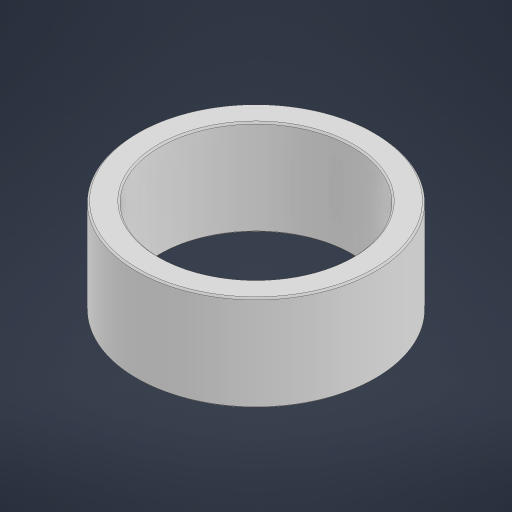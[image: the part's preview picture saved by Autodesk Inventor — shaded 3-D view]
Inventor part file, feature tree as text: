
AUTODESK INVENTOR PART (.ipt)
format: ipt  version: 2023 (Build 270158000, 158)  size: 179,712 bytes
history: native  units: in
note: dims shown in document units (in); Inventor stores cm internally (conversion verified against a paired STEP export)
features: chamfer x1
ambient origin geometry x8: Origin, YZ Plane, XZ Plane, XY Plane, X Axis, Y Axis, Z Axis, Center Point
bodies: Solid1 (feature_tree)
feature tree (1):
  chamfer  "Chamfer1"  [1 undecoded]
note: 1 required parameter value undecoded (feature->parameter linkage not recoverable at this tier; creation-order binding heuristic only, values carry confidence <= 0.55)
